# Revit family: Coifa New Vetro 60
name_source: partatom
category: Equipamento mecânico
revit_build: Autodesk Revit 2014 (Build: 20130308_1515(x64)
units: mm (PartAtom-declared; Revit-internal decimal feet)

## types (2) — shared parameters
Altura da Extensão (máx 48cm) = 0.48
Atendimento ao Cliente = http://www.tramontina.com.br
Classe da Construção = CLASSE I
Descrição = Coifa de Parede New Vetro 60
Desenvolvedor da Biblioteca = Studio BIM
Disjuntor Termomagnético = 10 A
Frequência = 60 Hz
Grau de Proteção = IPX0
Iluminação = Lâmpadas LED - Cor 3200 K - 2 x 1,5 W - 12 V
Linha = Vetro
Nível de Ruído = 64 dB(A) - cfe. Norma EN 60704
Peso Bruto (Kg) = 18.7
Peso Líquido (Kg) = 15.1
Potência Elétrica = 225 W
Potência do Motor = 220 W
Produto = Coifa de Parede New Vetro 60
Segmento = Residencial
Site do Desenvolvedor = www.studiobim.arq.br
URL = http://www.tramontina.com.br
Vazão Máxima = 620 m3/h - cfe. Norma IEC 61591

## per-type parameters (varying)
| type | Código da Peça | Modelo | Tensão |
| 127 Volts | 95800/005 | 95800/005 | 127 V |
| 220 Volts | 95800/006 | 95800/006 | 220 V |

## geometry (parser evidence)
native form markers: Sweep x1
no freeform markers — native parametric forms only
